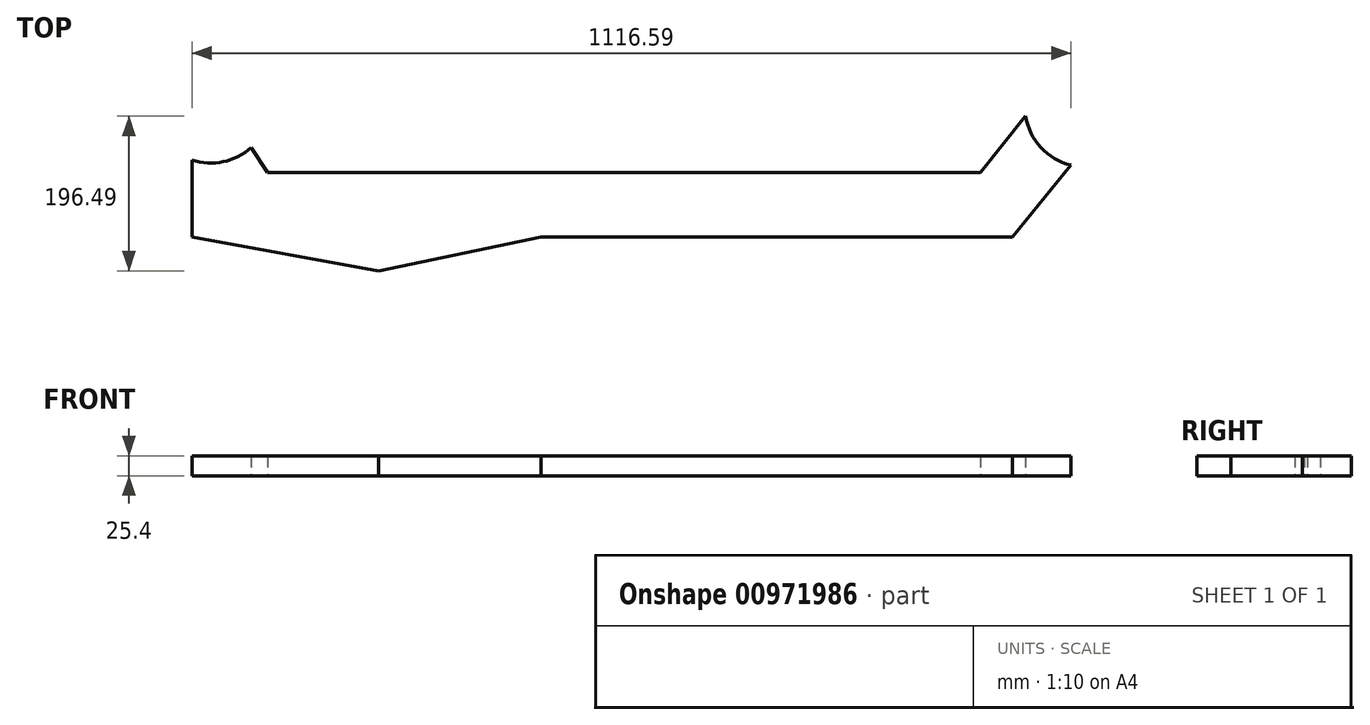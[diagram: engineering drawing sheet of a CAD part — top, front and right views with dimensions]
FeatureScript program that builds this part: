
annotation { "Feature Type Name" : "Feature", "Feature Type Description" : "" }
export const myFeature = defineFeature(function(context is Context, id is Id, definition is map)
    precondition{}
    {
        {
            var Q0;
            Q0=qCreatedBy(makeId("Top.planeOp"),FACE);
            var sketch = newSketch(context, id + "F0", { "sketchPlane" : qUnion([Q0])});
            skLineSegment(sketch, "E0", {"start": v(-598.63, -26.69) * mm, "end": v(-21.24, -26.69) * mm});
            skLineSegment(sketch, "E1", {"start": v(-598.63, -26.69) * mm, "end": v(-361.45, -69.8) * mm});
            skLineSegment(sketch, "E2", {"start": v(-361.45, -69.8) * mm, "end": v(-155.4, -26.69) * mm});
            skLineSegment(sketch, "E3", {"start": v(-16.3, 54.8) * mm, "end": v(402.96, 54.8) * mm});
            skLineSegment(sketch, "E4", {"start": v(-21.24, -26.69) * mm, "end": v(398.02, -26.69) * mm});
            skLineSegment(sketch, "E5", {"start": v(398.02, -26.69) * mm, "end": v(443.54, -26.69) * mm});
            skLineSegment(sketch, "E6", {"start": v(443.54, -26.69) * mm, "end": v(517.96, 64.39) * mm});
            skLineSegment(sketch, "E7", {"start": v(402.96, 54.8) * mm, "end": v(460.46, 126.68) * mm});
            skArc(sketch, "E8", {"start": v(460.46, 126.68) * mm, "mid": v(479.75, 86.8) * mm, "end": v(517.96, 64.39) * mm});
            skLineSegment(sketch, "E9", {"start": v(-502.67, 54.8) * mm, "end": v(-16.3, 54.8) * mm});
            skLineSegment(sketch, "E10", {"start": v(-598.63, -26.69) * mm, "end": v(-598.63, 20.61) * mm});
            skLineSegment(sketch, "E11", {"start": v(-598.63, 20.61) * mm, "end": v(-598.63, 70.76) * mm});
            skLineSegment(sketch, "E12", {"start": v(-502.67, 54.8) * mm, "end": v(-523.32, 87.01) * mm});
            skArc(sketch, "E13", {"start": v(-598.63, 70.76) * mm, "mid": v(-558.77, 68.67) * mm, "end": v(-523.32, 87.01) * mm});
            skSolve(sketch);
        }
        {
            var Q0;
            Q0=makeQuery(id+"F0.imprint","IMPRINT",FACE,{"disambiguationData":[TD([[makeQuery(id+"F0.imprint","IMPRINT",EDGE,{"derivedFrom":sQuery(id+"F0.wireOp",EDGE,"E3")}),-1.0]])]});
            var Q1;
            {var subQ0=sQuery(id+"F0.wireOp",EDGE,"E1");Q1=makeQuery(id+"F0.imprint","IMPRINT",FACE,{"disambiguationData":[TD([[makeQuery(id+"F0.imprint","IMPRINT",EDGE,{"derivedFrom":subQ0}),1.0]])]});}
            extrude(context, id + "F1", {"entities" : qUnion([Q0, Q1]), "depth" : 25.4 * mm, "offsetDistance" : 25.4 * mm});
        }
    });
